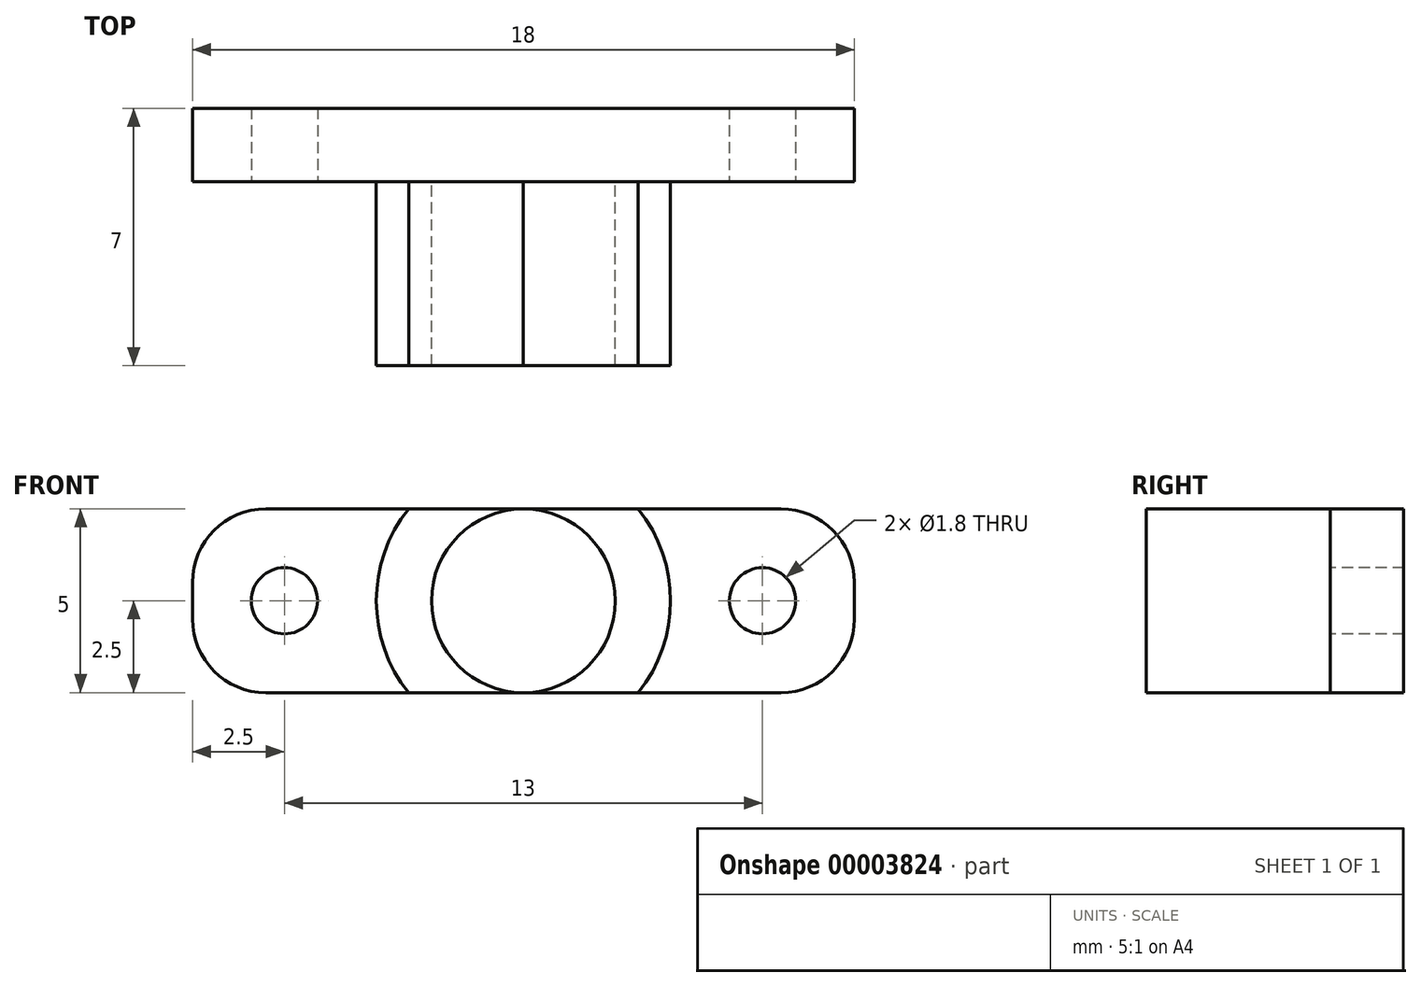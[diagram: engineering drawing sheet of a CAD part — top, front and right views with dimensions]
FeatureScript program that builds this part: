
annotation { "Feature Type Name" : "Feature", "Feature Type Description" : "" }
export const myFeature = defineFeature(function(context is Context, id is Id, definition is map)
    precondition{}
    {
        {
            var Q0;
            Q0=qCreatedBy(makeId("Front.planeOp"),FACE);
            var sketch = newSketch(context, id + "F0", { "sketchPlane" : qUnion([Q0])});
            skCircle(sketch, "E0", {"center": v(0, 0) * mm, "radius": 2.5 * mm});
            skArc(sketch, "E1", {"start": v(-3.12, 2.5) * mm, "mid": v(-4, 0) * mm, "end": v(-3.12, -2.5) * mm});
            skLineSegment(sketch, "E2", {"start": v(-3.12, 2.5) * mm, "end": v(3.12, 2.5) * mm});
            skLineSegment(sketch, "E3", {"start": v(3.12, -2.5) * mm, "end": v(-3.12, -2.5) * mm});
            skArc(sketch, "E4.trimOffspring", {"start": v(3.12, -2.5) * mm, "mid": v(4, 0) * mm, "end": v(3.12, 2.5) * mm});
            skSolve(sketch);
        }
        {
            var Q0;
            {var subQ0=sQuery(id+"F0.wireOp",EDGE,"E4.trimOffspring");Q0=makeQuery(id+"F0.imprint","IMPRINT",FACE,{"disambiguationData":[TD([[makeQuery(id+"F0.imprint","IMPRINT",EDGE,{"derivedFrom":subQ0}),1.0]])]});}
            var Q1;
            {var subQ3=sQuery(id+"F0.wireOp",EDGE,"E1");Q1=makeQuery(id+"F0.imprint","IMPRINT",FACE,{"disambiguationData":[TD([[makeQuery(id+"F0.imprint","IMPRINT",EDGE,{"derivedFrom":subQ3}),1.0]])]});}
            extrude(context, id + "F1", {"entities" : qUnion([Q0, Q1]), "depth" : 5 * mm});
        }
        {
            var Q0;
            Q0=qCreatedBy(makeId("Front.planeOp"),FACE);
            var sketch = newSketch(context, id + "F2", { "sketchPlane" : qUnion([Q0])});
            skLineSegment(sketch, "E5.rect.bottom", {"start": v(9, 2.5) * mm, "end": v(-9, 2.5) * mm});
            skLineSegment(sketch, "E5.rect.top", {"start": v(9, -2.5) * mm, "end": v(-9, -2.5) * mm});
            skLineSegment(sketch, "E5.rect.left", {"start": v(9, 2.5) * mm, "end": v(9, -2.5) * mm});
            skLineSegment(sketch, "E5.rect.right", {"start": v(-9, 2.5) * mm, "end": v(-9, -2.5) * mm});
            skPoint(sketch, "E5.rect.middle", {"position": v(0, 0) * mm});
            skCircle(sketch, "E6", {"center": v(-6.5, 0) * mm, "radius": 0.9 * mm});
            skCircle(sketch, "E7", {"center": v(6.5, 0) * mm, "radius": 0.9 * mm});
            skSolve(sketch);
        }
        {
            var Q0;
            Q0 = qSketchRegion(id + "F2", true);
            extrude(context, id + "F3", {"entities" : qUnion([Q0]), "oppositeDirection" : true, "depth" : 2 * mm});
        }
        {
            var Q0;
            Q0=makeQuery(id+"F3.opExtrude","SWEPT_EDGE",EDGE,{"disambiguationData":[OSD([sQuery(id+"F2.wireOp",EDGE,"E5.rect.bottom"),sQuery(id+"F2.wireOp",EDGE,"E5.rect.right")])]});
            var Q1;
            Q1=makeQuery(id+"F3.opExtrude","SWEPT_EDGE",EDGE,{"disambiguationData":[OSD([sQuery(id+"F2.wireOp",EDGE,"E5.rect.bottom"),sQuery(id+"F2.wireOp",EDGE,"E5.rect.left")])]});
            var Q2;
            Q2=makeQuery(id+"F3.opExtrude","SWEPT_EDGE",EDGE,{"disambiguationData":[OSD([sQuery(id+"F2.wireOp",EDGE,"E5.rect.top"),sQuery(id+"F2.wireOp",EDGE,"E5.rect.left")])]});
            var Q3;
            Q3=makeQuery(id+"F3.opExtrude","SWEPT_EDGE",EDGE,{"disambiguationData":[OSD([sQuery(id+"F2.wireOp",EDGE,"E5.rect.top"),sQuery(id+"F2.wireOp",EDGE,"E5.rect.right")])]});
            fillet(context, id + "F4", {"entities" : qUnion([Q0, Q1, Q2, Q3]), "radius" : 2 * mm, "tangentPropagation" : true, "allowEdgeOverflow" : false});
        }
    });
